# Revit family: Building-IEC309Boards-GEWISS-68QDIN-DISTRIBUTION-BOARD-10MOD_2SOCKET-OUTLETS_IB_VERT
name_source: partatom
category: Apparecchi elettrici
units: mm (PartAtom-declared; Revit-internal decimal feet)

## family parameters
Condiviso = No
Host = Superficie
Mantenere orientamento annotazione = Sì
Punto di calcolo locali = Sì
Quota connettore circolare = Usa diametro
Taglio con vuoti quando caricato = No
Tipo di parte = Normale

## types (1)
- GW68025N - Q-DIN 10M.2 FLANGES S.O.BL.VR.SBF IP65
    Accordance with Standards = EN 60208 - EN 60670-1 - IEC 60670-24
    Catalogue = BUILDING
    Catalogue Range = 68 QDIN
    Colour = Grey RAL 7035
    Descrizione = Q-DIN 10M.2 FLANGES S.O.BL.VR.SBF IP65
    Dispersible power A (W) = 16
    Dispersible power B (W) = 42
    EAN code = 8011564750456
    Electrocod = 2242
    Glow Wire Test = 650°C
    Houseable interloc. socket. = 2 IB Vert. 16-32A IP67
    Houseable socket = 2 IB Vert. 16-32A IP67
    IDF = 8d8d5ddc-ceb7-4ae3-b9f4-e87bff064777
    IDT = 0e75038c-3d4e-49ed-b410-1e2ae7ccf8d5
    IP degree = IP65
    Immagine tipo = GW68025N.jpg
    Installation type = Surface-mounting
    Insulation class = II
    L_Moduli = 190 mm  [stored 0.62336 ft]
    Modello = GW68025N
    No. IB socket-outlets houseable = 2 IB Vert. 16-32A IP67
    No. of blank lids supplied = 1 IB 16/32A
    No. of modules EN 50022 = 10
    No. of provided blank lids = 1 IB 16/32A
    Operating temperature: = -25 +40 °C
    POMELLO = bianco
    PRESA = rosso
    Produttore = GEWISS S.p.A.
    Prospetto di default = 1219 mm
    SEO = Board
    STRUTTURA = RAL - 7035
    STRUTTURA ALTA = Poche
    Shock resistance = IK08
    Spostamento_S = 1000 mm  [stored 3.28084 ft]
    Technical sheet = https://www.gewiss.com
    Thermo-pressure with ball = 70
    URL = https://www.gewiss.com
    VETRO = Vetro
    Version file RFA = 21.5
    Version type = Empty
    Working temperature = -25 ÷ +40 °C
    dist_barra din = 18 mm  [stored 0.0590551 ft]

note: source unit labels omitted for Thermo-pressure with ball — the stored unit's dimension contradicts the parameter name (converter mislabeling)

note: [stored X ft] marks values corroborated as IEEE doubles in the binary element streams (Revit-internal decimal feet)

## geometry (parser evidence)
native form markers: Sweep x4
no freeform markers — native parametric forms only
